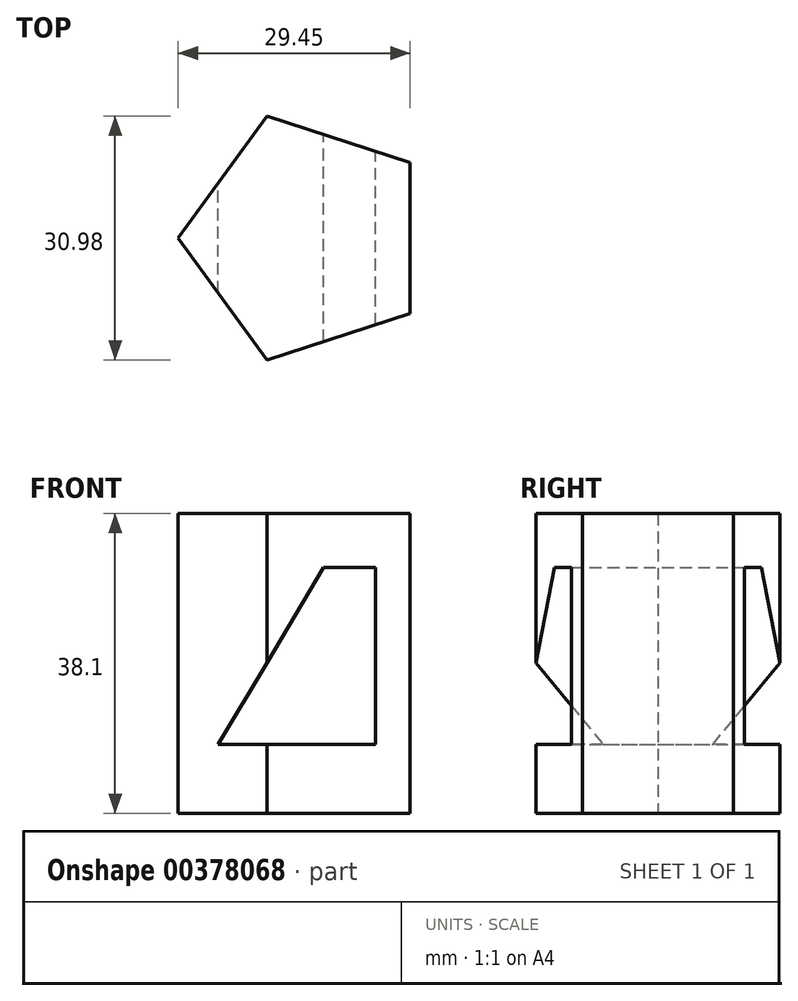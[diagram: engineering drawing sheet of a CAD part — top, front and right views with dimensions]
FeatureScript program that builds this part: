
annotation { "Feature Type Name" : "Feature", "Feature Type Description" : "" }
export const myFeature = defineFeature(function(context is Context, id is Id, definition is map)
    precondition{}
    {
        {
            var Q0;
            Q0=qCreatedBy(makeId("Top.planeOp"),FACE);
            var sketch = newSketch(context, id + "F0", { "sketchPlane" : qUnion([Q0])});
            skCircle(sketch, "E0.cCircle", {"center": v(0, 0) * mm, "radius": 13.17 * mm, "construction": true});
            skLineSegment(sketch, "E0.0", {"start": v(13.17, 9.57) * mm, "end": v(13.17, -9.57) * mm});
            skLineSegment(sketch, "E0.1", {"start": v(13.17, -9.57) * mm, "end": v(-5.03, -15.49) * mm});
            skLineSegment(sketch, "E0.2", {"start": v(-5.03, -15.49) * mm, "end": v(-16.28, 0) * mm});
            skLineSegment(sketch, "E0.3", {"start": v(-16.28, 0) * mm, "end": v(-5.03, 15.49) * mm});
            skLineSegment(sketch, "E0.4", {"start": v(-5.03, 15.49) * mm, "end": v(13.17, 9.57) * mm});
            skPoint(sketch, "E0.0.midPoint", {"position": v(13.17, 0) * mm});
            skSolve(sketch);
        }
        {
            var Q0;
            Q0=makeQuery(id+"F0.imprint","IMPRINT",FACE,{"disambiguationData":[TD([[makeQuery(id+"F0.imprint","IMPRINT",EDGE,{"derivedFrom":sQuery(id+"F0.wireOp",EDGE,"E0.0")}),-1.0]])]});
            extrude(context, id + "F1", {"entities" : qUnion([Q0]), "depth" : 38.1 * mm});
        }
        {
            var Q0;
            Q0=qCreatedBy(makeId("Front.planeOp"),FACE);
            var sketch = newSketch(context, id + "F2", { "sketchPlane" : qUnion([Q0])});
            skLineSegment(sketch, "E1", {"start": v(2.2, 31.22) * mm, "end": v(8.78, 31.22) * mm});
            skLineSegment(sketch, "E2", {"start": v(8.78, 31.22) * mm, "end": v(8.78, 8.78) * mm});
            skLineSegment(sketch, "E3", {"start": v(8.78, 8.78) * mm, "end": v(-11.22, 8.78) * mm});
            skLineSegment(sketch, "E4", {"start": v(-11.22, 8.78) * mm, "end": v(2.2, 31.22) * mm});
            skSolve(sketch);
        }
        {
            var Q0;
            Q0 = qSketchRegion(id + "F2", true);
            extrude(context, id + "F3", {"entities" : qUnion([Q0]), "operationType" : NewBodyOperationType.REMOVE, "endBound" : BoundingType.SYMMETRIC, "depth" : 55.37 * mm});
        }
    });
